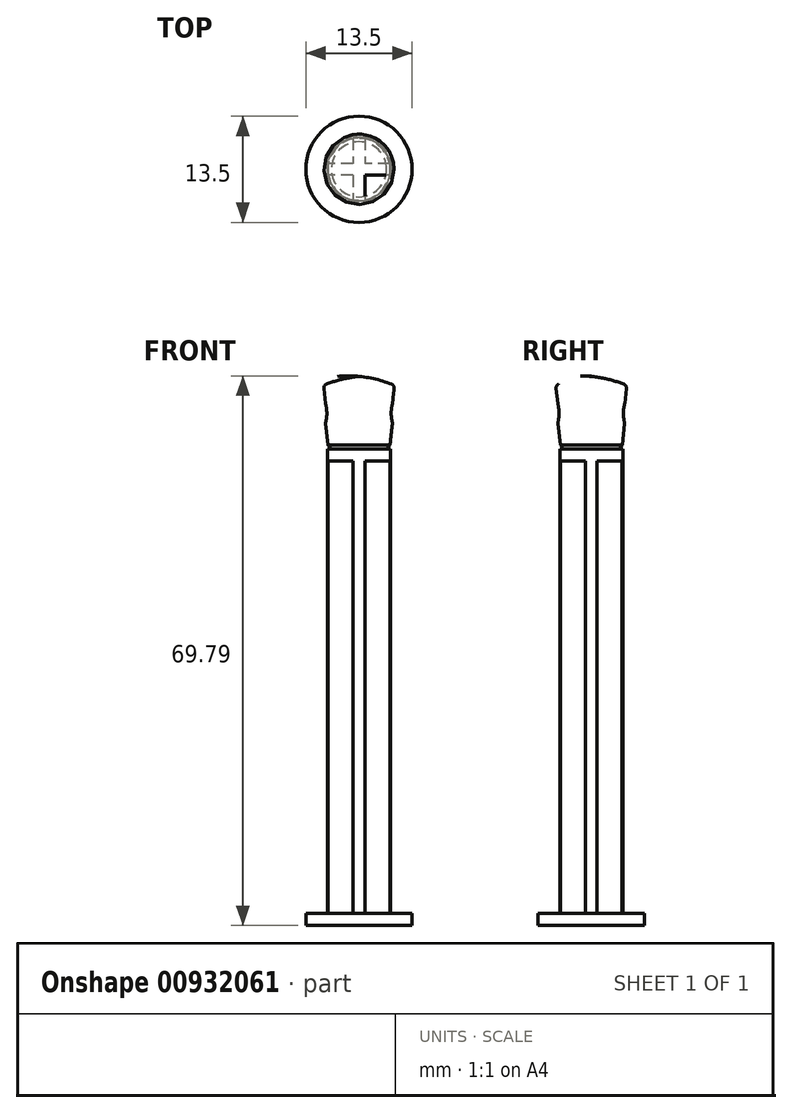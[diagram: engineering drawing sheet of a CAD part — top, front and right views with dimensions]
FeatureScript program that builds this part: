
annotation { "Feature Type Name" : "Feature", "Feature Type Description" : "" }
export const myFeature = defineFeature(function(context is Context, id is Id, definition is map)
    precondition{}
    {
        {
            var Q0;
            Q0=qCreatedBy(makeId("Top.planeOp"),FACE);
            var sketch = newSketch(context, id + "F0", { "sketchPlane" : qUnion([Q0])});
            skLineSegment(sketch, "E0.bottom", {"start": v(3.93, -0.75) * mm, "end": v(0.75, -0.75) * mm});
            skLineSegment(sketch, "E0.top", {"start": v(3.93, 0.75) * mm, "end": v(0.75, 0.75) * mm});
            skPoint(sketch, "E0.middle", {"position": v(0, 0) * mm});
            skLineSegment(sketch, "E1.left", {"start": v(0.75, 3.93) * mm, "end": v(0.75, 0.75) * mm});
            skLineSegment(sketch, "E1.right", {"start": v(-0.75, 3.93) * mm, "end": v(-0.75, 0.75) * mm});
            skLineSegment(sketch, "E2.trimOffspring", {"start": v(-0.75, -0.75) * mm, "end": v(-0.75, -3.93) * mm});
            skLineSegment(sketch, "E3.trimOffspring", {"start": v(-0.75, 0.75) * mm, "end": v(-3.93, 0.75) * mm});
            skLineSegment(sketch, "E4.trimOffspring", {"start": v(0.75, -0.75) * mm, "end": v(0.75, -3.93) * mm});
            skLineSegment(sketch, "E5.trimOffspring", {"start": v(-0.75, -0.75) * mm, "end": v(-3.93, -0.75) * mm});
            skCircle(sketch, "E6", {"center": v(0, 0) * mm, "radius": 6.75 * mm});
            skArc(sketch, "E7", {"start": v(0.75, 3.93) * mm, "mid": v(0, 4) * mm, "end": v(-0.75, 3.93) * mm});
            skPoint(sketch, "E8.orphan", {"position": v(-0.75, 4) * mm});
            skPoint(sketch, "E1.bottom.start.orphan", {"position": v(0.75, 4) * mm});
            skArc(sketch, "E9.trimOffspring", {"start": v(-3.93, 0.75) * mm, "mid": v(-4, 0) * mm, "end": v(-3.93, -0.75) * mm});
            skPoint(sketch, "E10.orphan", {"position": v(4, -0.75) * mm});
            skPoint(sketch, "E11.orphan", {"position": v(4, 0.75) * mm});
            skArc(sketch, "E12.trimOffspring", {"start": v(3.93, -0.75) * mm, "mid": v(4, 0) * mm, "end": v(3.93, 0.75) * mm});
            skPoint(sketch, "E13.orphan", {"position": v(0.75, -4) * mm});
            skPoint(sketch, "E14.orphan", {"position": v(-0.75, -4) * mm});
            skArc(sketch, "E15.trimOffspring", {"start": v(-0.75, -3.93) * mm, "mid": v(0, -4) * mm, "end": v(0.75, -3.93) * mm});
            skPoint(sketch, "E16.orphan", {"position": v(-4, 0.75) * mm});
            skPoint(sketch, "E17.orphan", {"position": v(-4, -0.75) * mm});
            skSolve(sketch);
        }
        {
            var Q0;
            Q0=makeQuery(id+"F0.imprint","IMPRINT",FACE,{"disambiguationData":[TD([[makeQuery(id+"F0.imprint","IMPRINT",EDGE,{"derivedFrom":sQuery(id+"F0.wireOp",EDGE,"E0.bottom")}),-1.0]])]});
            extrude(context, id + "F1", {"entities" : qUnion([Q0]), "depth" : 59 * mm, "offsetDistance" : 25 * mm});
        }
        {
            var Q0;
            Q0=makeQuery(id+"F0.imprint","IMPRINT",FACE,{"disambiguationData":[TD([[makeQuery(id+"F0.imprint","IMPRINT",EDGE,{"derivedFrom":sQuery(id+"F0.wireOp",EDGE,"E0.bottom")}),1.0]])]});
            extrude(context, id + "F2", {"entities" : qUnion([Q0]), "operationType" : NewBodyOperationType.ADD, "depth" : 1.5 * mm, "offsetDistance" : 25 * mm});
        }
        {
            var Q0;
            Q0=makeQuery(id+"F1.opExtrude","CAP_FACE",FACE,{"disambiguationData":[OSD([sQuery(id+"F0.wireOp",EDGE,"E0.bottom"),sQuery(id+"F0.wireOp",EDGE,"E0.top"),sQuery(id+"F0.wireOp",EDGE,"E1.left"),sQuery(id+"F0.wireOp",EDGE,"E1.right"),sQuery(id+"F0.wireOp",EDGE,"E2.trimOffspring"),sQuery(id+"F0.wireOp",EDGE,"E3.trimOffspring"),sQuery(id+"F0.wireOp",EDGE,"E4.trimOffspring"),sQuery(id+"F0.wireOp",EDGE,"E5.trimOffspring"),sQuery(id+"F0.wireOp",EDGE,"E7"),sQuery(id+"F0.wireOp",EDGE,"E9.trimOffspring"),sQuery(id+"F0.wireOp",EDGE,"E12.trimOffspring"),sQuery(id+"F0.wireOp",EDGE,"E15.trimOffspring")])],"isStart":false});
            var sketch = newSketch(context, id + "F3", { "sketchPlane" : qUnion([Q0])});
            skCircle(sketch, "E18", {"center": v(0, 0) * mm, "radius": 4 * mm});
            skSolve(sketch);
        }
        {
            var Q0;
            {var subQ1=makeQuery(id+"F1.opExtrude","CAP_EDGE",EDGE,{"disambiguationData":[OSD([sQuery(id+"F0.wireOp",EDGE,"E0.top")])],"isStart":false});Q0=makeQuery(id+"F3.imprint","IMPRINT",FACE,{"disambiguationData":[TD([[makeQuery(id+"F3.imprint","IMPRINT",EDGE,{"derivedFrom":subQ1}),-1.0]])]});}
            var Q1;
            {var subQ1=makeQuery(id+"F1.opExtrude","CAP_EDGE",EDGE,{"disambiguationData":[OSD([sQuery(id+"F0.wireOp",EDGE,"E0.bottom")])],"isStart":false});Q1=makeQuery(id+"F3.imprint","IMPRINT",FACE,{"disambiguationData":[TD([[makeQuery(id+"F3.imprint","IMPRINT",EDGE,{"derivedFrom":subQ1}),1.0]])]});}
            var Q2;
            {var subQ2=makeQuery(id+"F1.opExtrude","CAP_EDGE",EDGE,{"disambiguationData":[OSD([sQuery(id+"F0.wireOp",EDGE,"E0.bottom")])],"isStart":false});Q2=makeQuery(id+"F3.imprint","IMPRINT",FACE,{"disambiguationData":[TD([[makeQuery(id+"F3.imprint","IMPRINT",EDGE,{"derivedFrom":subQ2}),-1.0]])]});}
            var Q3;
            {var subQ1=makeQuery(id+"F1.opExtrude","CAP_EDGE",EDGE,{"disambiguationData":[OSD([sQuery(id+"F0.wireOp",EDGE,"E1.right")])],"isStart":false});Q3=makeQuery(id+"F3.imprint","IMPRINT",FACE,{"disambiguationData":[TD([[makeQuery(id+"F3.imprint","IMPRINT",EDGE,{"derivedFrom":subQ1}),-1.0]])]});}
            var Q4;
            {var subQ1=makeQuery(id+"F1.opExtrude","CAP_EDGE",EDGE,{"disambiguationData":[OSD([sQuery(id+"F0.wireOp",EDGE,"E2.trimOffspring")])],"isStart":false});Q4=makeQuery(id+"F3.imprint","IMPRINT",FACE,{"disambiguationData":[TD([[makeQuery(id+"F3.imprint","IMPRINT",EDGE,{"derivedFrom":subQ1}),-1.0]])]});}
            extrude(context, id + "F4", {"entities" : qUnion([Q0, Q1, Q2, Q3, Q4]), "operationType" : NewBodyOperationType.ADD, "depth" : 1.5 * mm, "offsetDistance" : 25 * mm});
        }
        {
            var Q0;
            Q0=qCreatedBy(makeId("Front.planeOp"),FACE);
            var sketch = newSketch(context, id + "F5", { "sketchPlane" : qUnion([Q0])});
            skLineSegment(sketch, "E19", {"start": v(0, 56.57) * mm, "end": v(0, 71.57) * mm, "construction": true});
            skLineSegment(sketch, "E20.0", {"start": v(0, 60.5) * mm, "end": v(3.5, 60.5) * mm});
            skLineSegment(sketch, "E21", {"start": v(3.5, 60.5) * mm, "end": v(3.94, 61) * mm});
            skLineSegment(sketch, "E22", {"start": v(3.94, 61) * mm, "end": v(4.25, 63.81) * mm});
            skArc(sketch, "E23", {"start": v(4.25, 66.25) * mm, "mid": v(4.09, 65.03) * mm, "end": v(4.25, 63.81) * mm});
            skLineSegment(sketch, "E24", {"start": v(4.25, 66.25) * mm, "end": v(4.5, 68.6) * mm});
            skLineSegment(sketch, "E25", {"start": v(0, 69.73) * mm, "end": v(0, 60.5) * mm});
            skArc(sketch, "E26", {"start": v(4.5, 68.6) * mm, "mid": v(2.3, 69.34) * mm, "end": v(0, 69.73) * mm});
            skSolve(sketch);
        }
        {
            var Q0;
            Q0=makeQuery(id+"F5.imprint","IMPRINT",FACE,{"disambiguationData":[TD([[makeQuery(id+"F5.imprint","IMPRINT",EDGE,{"derivedFrom":sQuery(id+"F5.wireOp",EDGE,"E20.0")}),1.0]])]});
            var Q1;
            Q1=sQuery(id+"F5.wireOp",EDGE,"E19");
            revolve(context, id + "F6", {"operationType" : NewBodyOperationType.ADD, "surfaceOperationType" : NewSurfaceOperationType.NEW, "entities" : qUnion([Q0]), "axis" : qUnion([Q1]), "revolveType" : RevolveType.FULL});
        }
        {
            var Q0;
            Q0=makeQuery(id+"F6.opRevolve","SWEPT_EDGE",EDGE,{"disambiguationData":[OSD([sQuery(id+"F5.wireOp",EDGE,"E24"),sQuery(id+"F5.wireOp",EDGE,"E4JuSET1-0rR8-NZVl-g7PE-xko0uVOmy887")])]});
            var Q1;
            Q1=makeQuery(id+"F6.opRevolve","SWEPT_EDGE",EDGE,{"disambiguationData":[OSD([sQuery(id+"F5.wireOp",EDGE,"E23"),sQuery(id+"F5.wireOp",EDGE,"E24")])]});
            var Q2;
            Q2=makeQuery(id+"F6.opRevolve","SWEPT_EDGE",EDGE,{"disambiguationData":[OSD([sQuery(id+"F5.wireOp",EDGE,"E22"),sQuery(id+"F5.wireOp",EDGE,"E23")])]});
            fillet(context, id + "F7", {"entities" : qUnion([Q0, Q1, Q2]), "radius" : .5 * mm, "tangentPropagation" : true, "allowEdgeOverflow" : false});
        }
    });
